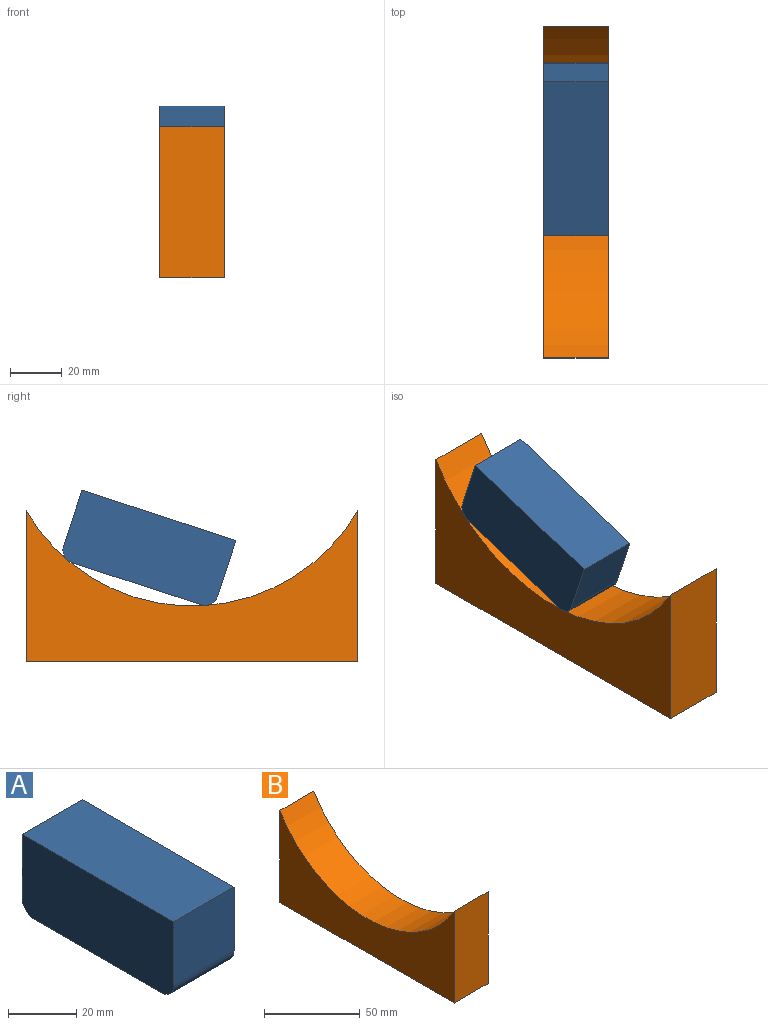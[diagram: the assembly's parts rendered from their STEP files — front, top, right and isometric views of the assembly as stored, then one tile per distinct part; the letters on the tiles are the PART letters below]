
ASSEMBLY  parts=2 mates=1
PART A: 8 faces, bbox 25x62.7x27.9 mm
  f0: plane 62.74x25mm, normal (0,0,1), area 1568.6mm2, adj f1,f5,f6,f7
  f1: plane 25x22.92mm, normal (0,-1,0), area 573mm2, adj f0,f2,f6,f7
  f2: cylinder r=5mm len=25mm, axis (-1,0,0), area 196.3mm2, adj f1,f3,f6,f7
  f3: plane 52.74x25mm, normal (0,0,-1), area 1318.6mm2, adj f2,f4,f6,f7
  f4: cylinder r=5mm len=25mm, axis (-1,0,0), area 196.3mm2, adj f3,f5,f6,f7
  f5: plane 25x22.92mm, normal (0,1,0), area 573mm2, adj f0,f4,f6,f7
  f6: plane 62.74x27.92mm, normal (1,0,0), area 1741.1mm2, adj f0,f1,f2,f3,f4,f5
  f7: plane 62.74x27.92mm, normal (-1,0,0), area 1741.1mm2, adj f0,f1,f2,f3,f4,f5
PART B: 6 faces, bbox 25x128.5x58.6 mm
  f0: cylinder r=74.35mm len=128.45mm, axis (-1,0,0), area 3876.7mm2, adj f1,f3,f4,f5
  f1: plane 58.58x25mm, normal (0,-1,0), area 1464.4mm2, adj f0,f2,f4,f5
  f2: plane 128.45x25mm, normal (0,0,-1), area 3211.3mm2, adj f1,f3,f4,f5
  f3: plane 58.58x25mm, normal (0,1,0), area 1464.4mm2, adj f0,f2,f4,f5
  f4: plane 128.45x58.58mm, normal (1,0,0), area 4165.2mm2, adj f0,f1,f2,f3
  f5: plane 128.45x58.58mm, normal (-1,0,0), area 4165.2mm2, adj f0,f1,f2,f3
PLACE A rot(axis=(1,0,0),18.1deg) t=(0,11.63,1.85)mm
PLACE B at identity fixed
MATE revolute B.f0 <-> A.f7  axis (-1,0,0) through (0,0,37.45)mm
